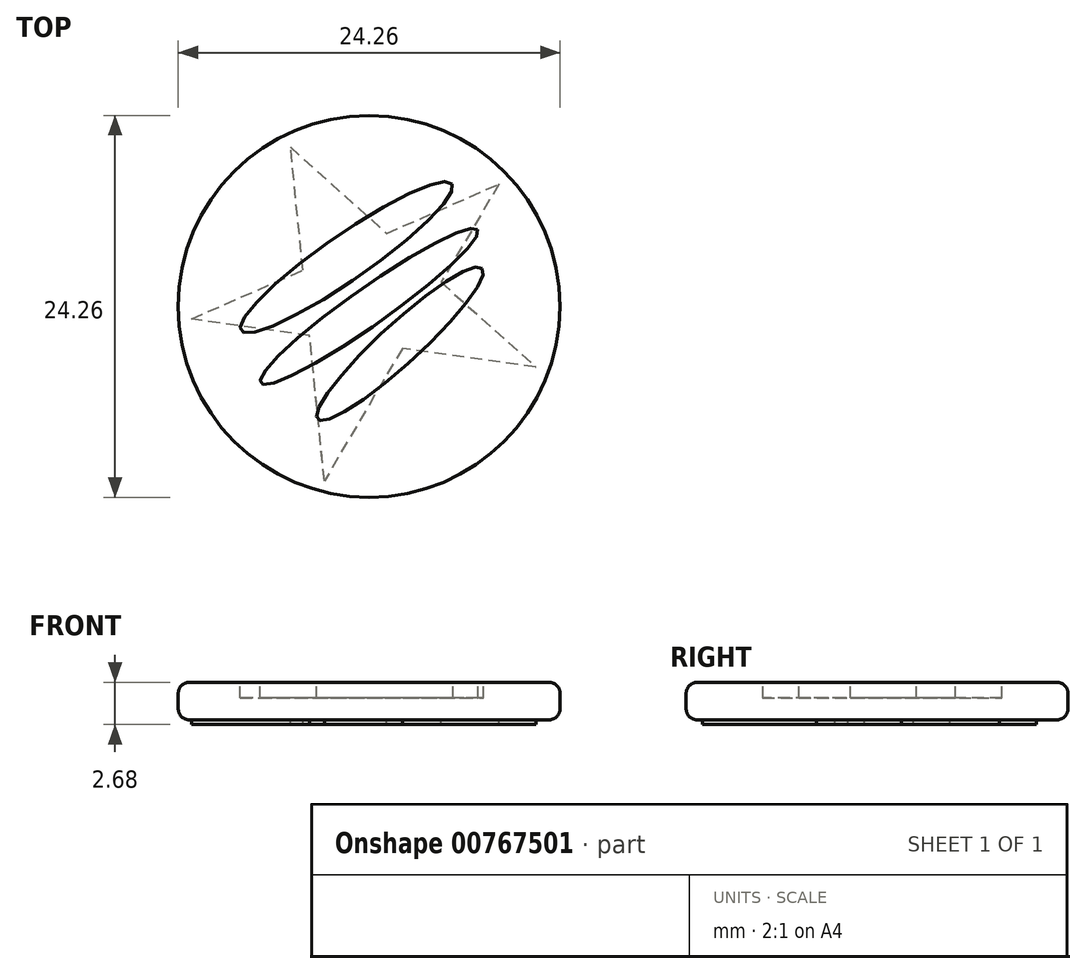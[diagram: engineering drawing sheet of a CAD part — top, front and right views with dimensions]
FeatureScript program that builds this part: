
annotation { "Feature Type Name" : "Feature", "Feature Type Description" : "" }
export const myFeature = defineFeature(function(context is Context, id is Id, definition is map)
    precondition{}
    {
        {
            var Q0;
            Q0=qCreatedBy(makeId("Top.planeOp"),FACE);
            var sketch = newSketch(context, id + "F0", { "sketchPlane" : qUnion([Q0])});
            skCircle(sketch, "E0", {"center": v(0, 0) * mm, "radius": 12.12 * mm});
            skSolve(sketch);
        }
        {
            var Q0;
            Q0=makeQuery(id+"F0.imprint","IMPRINT",FACE,{"disambiguationData":[TD([[makeQuery(id+"F0.imprint","IMPRINT",EDGE,{"derivedFrom":sQuery(id+"F0.wireOp",EDGE,"E0")}),1.0]])]});
            extrude(context, id + "F1", {"entities" : qUnion([Q0]), "depth" : 2.38 * mm, "offsetDistance" : 25 * mm});
        }
        {
            var Q0;
            Q0=makeQuery(id+"F1.opExtrude","CAP_EDGE",EDGE,{"disambiguationData":[OSD([sQuery(id+"F0.wireOp",EDGE,"E0")])],"isStart":false});
            var Q1;
            Q1=makeQuery(id+"F1.opExtrude","CAP_EDGE",EDGE,{"disambiguationData":[OSD([sQuery(id+"F0.wireOp",EDGE,"E0")])],"isStart":true});
            fillet(context, id + "F2", {"entities" : qUnion([Q0, Q1]), "radius" : 0.7 * mm, "tangentPropagation" : true, "allowEdgeOverflow" : false});
        }
        {
            var Q0;
            Q0=makeQuery(id+"F1.opExtrude","CAP_FACE",FACE,{"disambiguationData":[OSD([sQuery(id+"F0.wireOp",EDGE,"E0"),sQuery(id+"F0.wireOp",EDGE,"94177a11-9e2d-4171-8c38-329a05867a33"),sQuery(id+"F0.wireOp",EDGE,"1f29e8ec-964a-43c6-a6a5-c5f0c96d2577"),sQuery(id+"F0.wireOp",EDGE,"e5be4b2a-7039-47c3-bb76-cd9bf7615dd1")])],"isStart":false});
            var sketch = newSketch(context, id + "F3", { "sketchPlane" : qUnion([Q0])});
            skEllipse(sketch, "E1", {"center": v(-1.43, 3.12) * mm, "majorRadius": 8.16 * mm, "minorRadius": 1.44 * mm, "majorAxis": v(0.82, 0.57)});
            skEllipse(sketch, "E2", {"center": v(0, 0) * mm, "majorRadius": 8.44 * mm, "minorRadius": 1.19 * mm, "majorAxis": v(0.82, 0.58)});
            skEllipse(sketch, "E3", {"center": v(1.95, -2.38) * mm, "majorRadius": 7.1 * mm, "minorRadius": 1.27 * mm, "majorAxis": v(0.74, 0.68)});
            skText(sketch, "E4", { "text": "iiss gadda\n", "fontName": "OpenSans-Regular.ttf"});
            const initialGuessF3  = {"E4": [0.00094, -0.00685, 1, 0, 0.00123]};
            skSetInitialGuess(sketch, initialGuessF3);
            skSolve(sketch);
        }
        {
            var Q0;
            Q0=makeQuery(id+"F3.imprint","IMPRINT",FACE,{"disambiguationData":[TD([[makeQuery(id+"F3.imprint","IMPRINT",EDGE,{"derivedFrom":sQuery(id+"F3.wireOp",EDGE,"E1")}),1.0]])]});
            var Q1;
            Q1=makeQuery(id+"F3.imprint","IMPRINT",FACE,{"disambiguationData":[TD([[makeQuery(id+"F3.imprint","IMPRINT",EDGE,{"derivedFrom":sQuery(id+"F3.wireOp",EDGE,"E2")}),1.0]])]});
            var Q2;
            Q2=makeQuery(id+"F3.imprint","IMPRINT",FACE,{"disambiguationData":[TD([[makeQuery(id+"F3.imprint","IMPRINT",EDGE,{"derivedFrom":sQuery(id+"F3.wireOp",EDGE,"E3")}),1.0]])]});
            var Q3;
            Q3=sQuery(id+"F3.wireOp",EDGE,"E1");
            var Q4;
            Q4=sQuery(id+"F3.wireOp",EDGE,"E2");
            var Q5;
            Q5=sQuery(id+"F3.wireOp",EDGE,"E3");
            extrude(context, id + "F4", {"entities" : qUnion([Q0, Q1, Q2]), "operationType" : NewBodyOperationType.REMOVE, "surfaceEntities" : qUnion([Q3, Q4, Q5]), "oppositeDirection" : true, "depth" : 1 * mm, "offsetDistance" : 25 * mm});
        }
        {
            var Q0;
            Q0=qCreatedBy(makeId("Top.planeOp"),FACE);
            var sketch = newSketch(context, id + "F5", { "sketchPlane" : qUnion([Q0])});
            skLineSegment(sketch, "E5", {"start": v(-2.84, -11.1) * mm, "end": v(-5, 10.1) * mm});
            skLineSegment(sketch, "E6", {"start": v(-5, 10.1) * mm, "end": v(10.6, -3.85) * mm});
            skLineSegment(sketch, "E7", {"start": v(10.6, -3.85) * mm, "end": v(-11.28, -0.8) * mm});
            skLineSegment(sketch, "E8", {"start": v(-11.28, -0.8) * mm, "end": v(8.24, 7.76) * mm});
            skLineSegment(sketch, "E9", {"start": v(8.24, 7.76) * mm, "end": v(-2.84, -11.1) * mm});
            skSolve(sketch);
        }
        {
            var Q0;
            {var subQ0=sQuery(id+"F5.wireOp",EDGE,"E6");var subQ1=sQuery(id+"F5.wireOp",EDGE,"E5");var subQ2=makeQuery(id+"F5.imprint","INTERSECT",VERTEX,{"derivedFrom":[subQ1,subQ0]});Q0=makeQuery(id+"F5.imprint","IMPRINT",FACE,{"disambiguationData":[TD([[makeQuery(id+"F5.imprint","IMPRINT",EDGE,{"disambiguationData":[TD([[subQ2,1.0]])],"derivedFrom":subQ1}),-1.0]])]});}
            var Q1;
            {var subQ0=sQuery(id+"F5.wireOp",EDGE,"E8");var subQ1=sQuery(id+"F5.wireOp",EDGE,"E6");var subQ2=makeQuery(id+"F5.imprint","INTERSECT",VERTEX,{"derivedFrom":[subQ1,subQ0]});Q1=makeQuery(id+"F5.imprint","IMPRINT",FACE,{"disambiguationData":[TD([[makeQuery(id+"F5.imprint","IMPRINT",EDGE,{"disambiguationData":[TD([[subQ2,-1.0]])],"derivedFrom":subQ1}),1.0]])]});}
            var Q2;
            {var subQ1=sQuery(id+"F5.wireOp",EDGE,"E5");var subQ5=sQuery(id+"F5.wireOp",EDGE,"E7");var subQ6=makeQuery(id+"F5.imprint","INTERSECT",VERTEX,{"derivedFrom":[subQ1,subQ5]});Q2=makeQuery(id+"F5.imprint","IMPRINT",FACE,{"disambiguationData":[TD([[makeQuery(id+"F5.imprint","IMPRINT",EDGE,{"disambiguationData":[TD([[subQ6,-1.0]])],"derivedFrom":subQ1}),-1.0]])]});}
            var Q3;
            {var subQ0=sQuery(id+"F5.wireOp",EDGE,"E7");var subQ1=sQuery(id+"F5.wireOp",EDGE,"E5");var subQ2=makeQuery(id+"F5.imprint","INTERSECT",VERTEX,{"derivedFrom":[subQ1,subQ0]});Q3=makeQuery(id+"F5.imprint","IMPRINT",FACE,{"disambiguationData":[TD([[makeQuery(id+"F5.imprint","IMPRINT",EDGE,{"disambiguationData":[TD([[subQ2,-1.0]])],"derivedFrom":subQ1}),1.0]])]});}
            var Q4;
            {var subQ0=sQuery(id+"F5.wireOp",EDGE,"E7");var subQ1=sQuery(id+"F5.wireOp",EDGE,"E6");var subQ2=makeQuery(id+"F5.imprint","INTERSECT",VERTEX,{"derivedFrom":[subQ1,subQ0]});Q4=makeQuery(id+"F5.imprint","IMPRINT",FACE,{"disambiguationData":[TD([[makeQuery(id+"F5.imprint","IMPRINT",EDGE,{"disambiguationData":[TD([[subQ2,1.0]])],"derivedFrom":subQ1}),-1.0]])]});}
            var Q5;
            {var subQ0=sQuery(id+"F5.wireOp",EDGE,"E9");var subQ1=sQuery(id+"F5.wireOp",EDGE,"E5");var subQ2=makeQuery(id+"F5.imprint","INTERSECT",VERTEX,{"derivedFrom":[subQ1,subQ0]});Q5=makeQuery(id+"F5.imprint","IMPRINT",FACE,{"disambiguationData":[TD([[makeQuery(id+"F5.imprint","IMPRINT",EDGE,{"disambiguationData":[TD([[subQ2,-1.0]])],"derivedFrom":subQ1}),-1.0]])]});}
            extrude(context, id + "F6", {"entities" : qUnion([Q0, Q1, Q2, Q3, Q4, Q5]), "operationType" : NewBodyOperationType.ADD, "oppositeDirection" : true, "depth" : 0.3 * mm, "offsetDistance" : 25 * mm});
        }
    });
